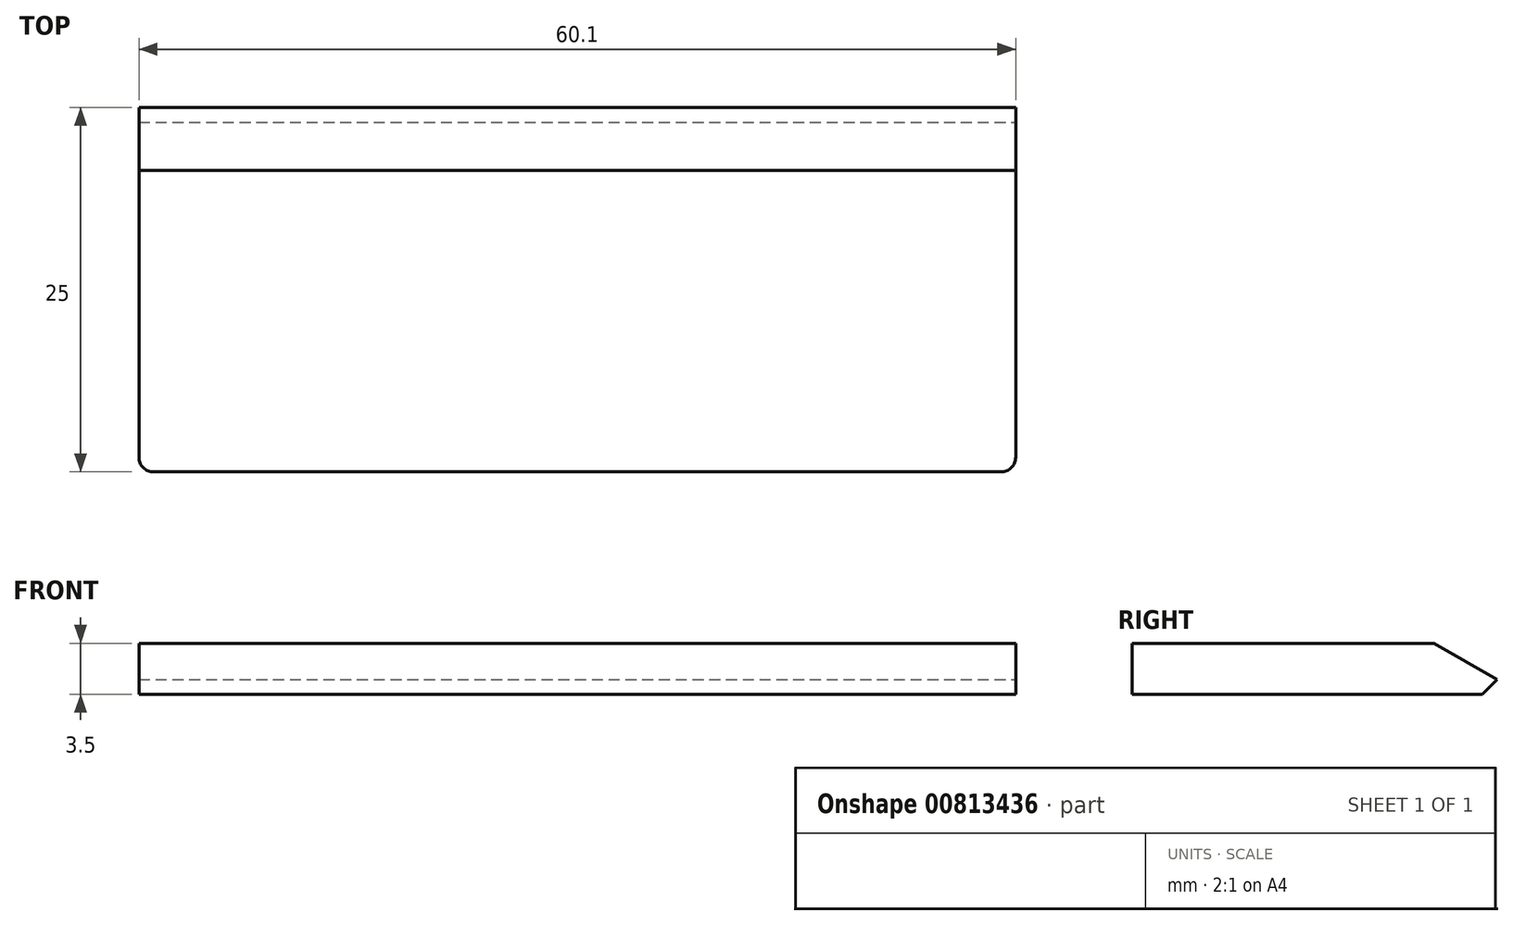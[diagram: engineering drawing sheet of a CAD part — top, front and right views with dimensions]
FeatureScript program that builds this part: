
annotation { "Feature Type Name" : "Feature", "Feature Type Description" : "" }
export const myFeature = defineFeature(function(context is Context, id is Id, definition is map)
    precondition{}
    {
        {
            var Q0;
            Q0=qCreatedBy(makeId("Top.planeOp"),FACE);
            var sketch = newSketch(context, id + "F0", { "sketchPlane" : qUnion([Q0])});
            skLineSegment(sketch, "E0.bottom", {"start": v(29.05, -12.5) * mm, "end": v(-29.05, -12.5) * mm});
            skLineSegment(sketch, "E0.top", {"start": v(30.05, 12.5) * mm, "end": v(-30.05, 12.5) * mm});
            skLineSegment(sketch, "E0.left", {"start": v(30.05, -11.5) * mm, "end": v(30.05, 12.5) * mm});
            skLineSegment(sketch, "E0.right", {"start": v(-30.05, -11.5) * mm, "end": v(-30.05, 12.5) * mm});
            skPoint(sketch, "E0.middle", {"position": v(0, 0) * mm});
            skPoint(sketch, "E1.visualSharp", {"position": v(30.05, 12.5) * mm});
            skLineSegment(sketch, "E1.filletArc", {"start": v(30.05, 12.5) * mm, "end": v(30.05, 12.5) * mm});
            skPoint(sketch, "E2.visualSharp", {"position": v(30.05, -12.5) * mm});
            skArc(sketch, "E2.filletArc", {"start": v(29.05, -12.5) * mm, "mid": v(29.76, -12.2) * mm, "end": v(30.05, -11.5) * mm});
            skPoint(sketch, "E3.visualSharp", {"position": v(-30.05, 12.5) * mm});
            skLineSegment(sketch, "E3.filletArc", {"start": v(-30.05, 12.5) * mm, "end": v(-30.05, 12.5) * mm});
            skPoint(sketch, "E4.visualSharp", {"position": v(-30.05, -12.5) * mm});
            skArc(sketch, "E4.filletArc", {"start": v(-30.05, -11.5) * mm, "mid": v(-29.76, -12.2) * mm, "end": v(-29.05, -12.5) * mm});
            skSolve(sketch);
        }
        {
            var Q0;
            Q0 = qSketchRegion(id + "F0", true);
            extrude(context, id + "F1", {"entities" : qUnion([Q0]), "endBound" : BoundingType.SYMMETRIC, "depth" : 3.5 * mm, "offsetDistance" : 25 * mm});
        }
        {
            var Q0;
            Q0=makeQuery(id+"F1.opExtrude","SWEPT_FACE",FACE,{"disambiguationData":[OSD([sQuery(id+"F0.wireOp",EDGE,"E0.left")])]});
            var sketch = newSketch(context, id + "F2", { "sketchPlane" : qUnion([Q0])});
            skLineSegment(sketch, "E5", {"start": v(11.5, -1.75) * mm, "end": v(12.5, -0.75) * mm});
            skLineSegment(sketch, "E6", {"start": v(12.5, -0.75) * mm, "end": v(8.17, 1.75) * mm});
            skLineSegment(sketch, "E7", {"start": v(11.5, -1.75) * mm, "end": v(13.17, -1.75) * mm});
            skLineSegment(sketch, "E8", {"start": v(13.17, -1.75) * mm, "end": v(13.17, 1.75) * mm});
            skLineSegment(sketch, "E9", {"start": v(13.17, 1.75) * mm, "end": v(8.17, 1.75) * mm});
            skSolve(sketch);
        }
        {
            var Q0;
            Q0 = qSketchRegion(id + "F2", true);
            extrude(context, id + "F3", {"entities" : qUnion([Q0]), "operationType" : NewBodyOperationType.REMOVE, "oppositeDirection" : true, "depth" : 100 * mm, "offsetDistance" : 25 * mm});
        }
    });
